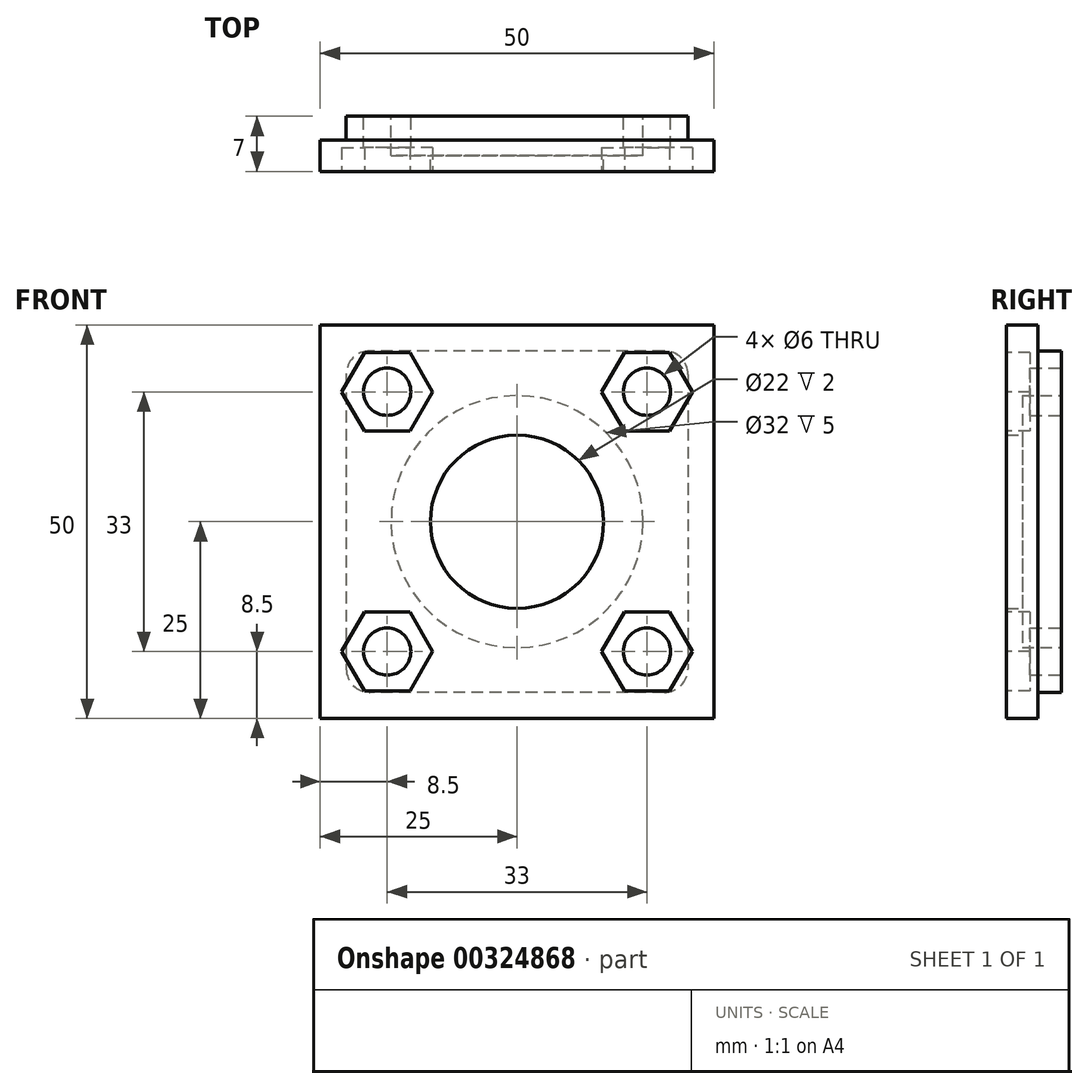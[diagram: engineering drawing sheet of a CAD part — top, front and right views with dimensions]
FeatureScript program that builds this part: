
annotation { "Feature Type Name" : "Feature", "Feature Type Description" : "" }
export const myFeature = defineFeature(function(context is Context, id is Id, definition is map)
    precondition{}
    {
        {
            var Q0;
            Q0=qCreatedBy(makeId("Front.planeOp"),FACE);
            var sketch = newSketch(context, id + "F0", { "sketchPlane" : qUnion([Q0])});
            skLineSegment(sketch, "E0.bottom", {"start": v(-25, 25) * mm, "end": v(25, 25) * mm});
            skLineSegment(sketch, "E0.top", {"start": v(-25, -25) * mm, "end": v(25, -25) * mm});
            skLineSegment(sketch, "E0.left", {"start": v(-25, 25) * mm, "end": v(-25, -25) * mm});
            skLineSegment(sketch, "E0.right", {"start": v(25, 25) * mm, "end": v(25, -25) * mm});
            skPoint(sketch, "E0.middle", {"position": v(0, 0) * mm});
            skSolve(sketch);
        }
        {
            var Q0;
            Q0=makeQuery(id+"F0.imprint","IMPRINT",FACE,{"disambiguationData":[TD([[makeQuery(id+"F0.imprint","IMPRINT",EDGE,{"derivedFrom":sQuery(id+"F0.wireOp",EDGE,"E0.bottom")}),-1.0]])]});
            extrude(context, id + "F1", {"entities" : qUnion([Q0]), "oppositeDirection" : true, "depth" : 4 * mm});
        }
        {
            var Q0;
            Q0=makeQuery(id+"F1.opExtrude","CAP_FACE",FACE,{"disambiguationData":[OSD([sQuery(id+"F0.wireOp",EDGE,"E0.bottom"),sQuery(id+"F0.wireOp",EDGE,"E0.top"),sQuery(id+"F0.wireOp",EDGE,"E0.left"),sQuery(id+"F0.wireOp",EDGE,"E0.right")])],"isStart":false});
            var sketch = newSketch(context, id + "F2", { "sketchPlane" : qUnion([Q0])});
            skLineSegment(sketch, "E1.bottom", {"start": v(-21.7, 21.7) * mm, "end": v(21.7, 21.7) * mm});
            skLineSegment(sketch, "E1.top", {"start": v(-21.7, -21.7) * mm, "end": v(21.7, -21.7) * mm});
            skLineSegment(sketch, "E1.left", {"start": v(-21.7, 21.7) * mm, "end": v(-21.7, -21.7) * mm});
            skLineSegment(sketch, "E1.right", {"start": v(21.7, 21.7) * mm, "end": v(21.7, -21.7) * mm});
            skPoint(sketch, "E1.middle", {"position": v(0, 0) * mm});
            skSolve(sketch);
        }
        {
            var Q0;
            Q0=makeQuery(id+"F2.imprint","IMPRINT",FACE,{"disambiguationData":[TD([[makeQuery(id+"F2.imprint","IMPRINT",EDGE,{"derivedFrom":sQuery(id+"F2.wireOp",EDGE,"E1.bottom")}),-1.0]])]});
            extrude(context, id + "F3", {"entities" : qUnion([Q0]), "operationType" : NewBodyOperationType.ADD, "depth" : 3 * mm});
        }
        {
            var Q0;
            Q0=makeQuery(id+"F3.opExtrude","CAP_FACE",FACE,{"disambiguationData":[OSD([sQuery(id+"F2.wireOp",EDGE,"E1.bottom"),sQuery(id+"F2.wireOp",EDGE,"E1.top"),sQuery(id+"F2.wireOp",EDGE,"E1.left"),sQuery(id+"F2.wireOp",EDGE,"E1.right")])],"isStart":false});
            var sketch = newSketch(context, id + "F4", { "sketchPlane" : qUnion([Q0])});
            skLineSegment(sketch, "E2", {"start": v(-21.7, 21.7) * mm, "end": v(21.7, -21.7) * mm, "construction": true});
            skLineSegment(sketch, "E3", {"start": v(21.7, 21.7) * mm, "end": v(-21.7, -21.7) * mm, "construction": true});
            skLineSegment(sketch, "E4.bottom", {"start": v(-16.5, 16.5) * mm, "end": v(16.5, 16.5) * mm, "construction": true});
            skLineSegment(sketch, "E4.top", {"start": v(-16.5, -16.5) * mm, "end": v(16.5, -16.5) * mm, "construction": true});
            skLineSegment(sketch, "E4.left", {"start": v(-16.5, 16.5) * mm, "end": v(-16.5, -16.5) * mm, "construction": true});
            skLineSegment(sketch, "E4.right", {"start": v(16.5, 16.5) * mm, "end": v(16.5, -16.5) * mm, "construction": true});
            skPoint(sketch, "E4.middle", {"position": v(0, 0) * mm});
            skCircle(sketch, "E5", {"center": v(-16.5, 16.5) * mm, "radius": 3 * mm});
            skCircle(sketch, "E6", {"center": v(16.5, 16.5) * mm, "radius": 3 * mm});
            skCircle(sketch, "E7", {"center": v(-16.5, -16.5) * mm, "radius": 3 * mm});
            skCircle(sketch, "E8", {"center": v(16.5, -16.5) * mm, "radius": 3 * mm});
            skCircle(sketch, "E9", {"center": v(0, 0) * mm, "radius": 11 * mm});
            skSolve(sketch);
        }
        {
            var Q0;
            Q0=makeQuery(id+"F4.imprint","IMPRINT",FACE,{"disambiguationData":[TD([[makeQuery(id+"F4.imprint","IMPRINT",EDGE,{"derivedFrom":sQuery(id+"F4.wireOp",EDGE,"E5")}),1.0]])]});
            var Q1;
            Q1=makeQuery(id+"F4.imprint","IMPRINT",FACE,{"disambiguationData":[TD([[makeQuery(id+"F4.imprint","IMPRINT",EDGE,{"derivedFrom":sQuery(id+"F4.wireOp",EDGE,"E6")}),1.0]])]});
            var Q2;
            Q2=makeQuery(id+"F4.imprint","IMPRINT",FACE,{"disambiguationData":[TD([[makeQuery(id+"F4.imprint","IMPRINT",EDGE,{"derivedFrom":sQuery(id+"F4.wireOp",EDGE,"E8")}),1.0]])]});
            var Q3;
            Q3=makeQuery(id+"F4.imprint","IMPRINT",FACE,{"disambiguationData":[TD([[makeQuery(id+"F4.imprint","IMPRINT",EDGE,{"derivedFrom":sQuery(id+"F4.wireOp",EDGE,"E7")}),1.0]])]});
            var Q4;
            Q4=makeQuery(id+"F4.imprint","IMPRINT",FACE,{"disambiguationData":[TD([[makeQuery(id+"F4.imprint","IMPRINT",EDGE,{"derivedFrom":sQuery(id+"F4.wireOp",EDGE,"E9")}),1.0]])]});
            extrude(context, id + "F5", {"entities" : qUnion([Q0, Q1, Q2, Q3, Q4]), "operationType" : NewBodyOperationType.REMOVE, "oppositeDirection" : true, "depth" : 25 * mm});
        }
        {
            var Q0;
            Q0=makeQuery(id+"F1.opExtrude","CAP_FACE",FACE,{"disambiguationData":[OSD([sQuery(id+"F0.wireOp",EDGE,"E0.bottom"),sQuery(id+"F0.wireOp",EDGE,"E0.top"),sQuery(id+"F0.wireOp",EDGE,"E0.left"),sQuery(id+"F0.wireOp",EDGE,"E0.right")])],"isStart":true});
            var sketch = newSketch(context, id + "F6", { "sketchPlane" : qUnion([Q0])});
            skCircle(sketch, "E10.cCircle", {"center": v(-16.5, 16.5) * mm, "radius": 5 * mm, "construction": true});
            skLineSegment(sketch, "E10.0", {"start": v(-13.61, 11.5) * mm, "end": v(-19.39, 11.5) * mm});
            skLineSegment(sketch, "E10.1", {"start": v(-19.39, 11.5) * mm, "end": v(-22.27, 16.5) * mm});
            skLineSegment(sketch, "E10.2", {"start": v(-22.27, 16.5) * mm, "end": v(-19.39, 21.5) * mm});
            skLineSegment(sketch, "E10.3", {"start": v(-19.39, 21.5) * mm, "end": v(-13.61, 21.5) * mm});
            skLineSegment(sketch, "E10.4", {"start": v(-13.61, 21.5) * mm, "end": v(-10.73, 16.5) * mm});
            skLineSegment(sketch, "E10.5", {"start": v(-10.73, 16.5) * mm, "end": v(-13.61, 11.5) * mm});
            skPoint(sketch, "E10.0.midPoint", {"position": v(-16.5, 11.5) * mm});
            skCircle(sketch, "E11.cCircle", {"center": v(-16.5, -16.5) * mm, "radius": 5 * mm, "construction": true});
            skLineSegment(sketch, "E11.0", {"start": v(-13.61, -21.5) * mm, "end": v(-19.39, -21.5) * mm});
            skLineSegment(sketch, "E11.1", {"start": v(-19.39, -21.5) * mm, "end": v(-22.27, -16.5) * mm});
            skLineSegment(sketch, "E11.2", {"start": v(-22.27, -16.5) * mm, "end": v(-19.39, -11.5) * mm});
            skLineSegment(sketch, "E11.3", {"start": v(-19.39, -11.5) * mm, "end": v(-13.61, -11.5) * mm});
            skLineSegment(sketch, "E11.4", {"start": v(-13.61, -11.5) * mm, "end": v(-10.73, -16.5) * mm});
            skLineSegment(sketch, "E11.5", {"start": v(-10.73, -16.5) * mm, "end": v(-13.61, -21.5) * mm});
            skPoint(sketch, "E11.0.midPoint", {"position": v(-16.5, -21.5) * mm});
            skCircle(sketch, "E12.cCircle", {"center": v(16.5, 16.5) * mm, "radius": 5 * mm, "construction": true});
            skLineSegment(sketch, "E12.0", {"start": v(13.61, 21.5) * mm, "end": v(19.39, 21.5) * mm});
            skLineSegment(sketch, "E12.1", {"start": v(19.39, 21.5) * mm, "end": v(22.27, 16.5) * mm});
            skLineSegment(sketch, "E12.2", {"start": v(22.27, 16.5) * mm, "end": v(19.39, 11.5) * mm});
            skLineSegment(sketch, "E12.3", {"start": v(19.39, 11.5) * mm, "end": v(13.61, 11.5) * mm});
            skLineSegment(sketch, "E12.4", {"start": v(13.61, 11.5) * mm, "end": v(10.73, 16.5) * mm});
            skLineSegment(sketch, "E12.5", {"start": v(10.73, 16.5) * mm, "end": v(13.61, 21.5) * mm});
            skPoint(sketch, "E12.0.midPoint", {"position": v(16.5, 21.5) * mm});
            skCircle(sketch, "E13.cCircle", {"center": v(16.5, -16.5) * mm, "radius": 5 * mm, "construction": true});
            skLineSegment(sketch, "E13.0", {"start": v(19.39, -21.5) * mm, "end": v(13.61, -21.5) * mm});
            skLineSegment(sketch, "E13.1", {"start": v(13.61, -21.5) * mm, "end": v(10.73, -16.5) * mm});
            skLineSegment(sketch, "E13.2", {"start": v(10.73, -16.5) * mm, "end": v(13.61, -11.5) * mm});
            skLineSegment(sketch, "E13.3", {"start": v(13.61, -11.5) * mm, "end": v(19.39, -11.5) * mm});
            skLineSegment(sketch, "E13.4", {"start": v(19.39, -11.5) * mm, "end": v(22.27, -16.5) * mm});
            skLineSegment(sketch, "E13.5", {"start": v(22.27, -16.5) * mm, "end": v(19.39, -21.5) * mm});
            skPoint(sketch, "E13.0.midPoint", {"position": v(16.5, -21.5) * mm});
            skSolve(sketch);
        }
        {
            var Q0;
            Q0=makeQuery(id+"F6.imprint","IMPRINT",FACE,{"disambiguationData":[TD([[makeQuery(id+"F6.imprint","IMPRINT",EDGE,{"derivedFrom":sQuery(id+"F6.wireOp",EDGE,"E10.0")}),-1.0]])]});
            var Q1;
            Q1=makeQuery(id+"F6.imprint","IMPRINT",FACE,{"disambiguationData":[TD([[makeQuery(id+"F6.imprint","IMPRINT",EDGE,{"derivedFrom":sQuery(id+"F6.wireOp",EDGE,"E12.0")}),-1.0]])]});
            var Q2;
            Q2=makeQuery(id+"F6.imprint","IMPRINT",FACE,{"disambiguationData":[TD([[makeQuery(id+"F6.imprint","IMPRINT",EDGE,{"derivedFrom":sQuery(id+"F6.wireOp",EDGE,"E13.0")}),-1.0]])]});
            var Q3;
            Q3=makeQuery(id+"F6.imprint","IMPRINT",FACE,{"disambiguationData":[TD([[makeQuery(id+"F6.imprint","IMPRINT",EDGE,{"derivedFrom":sQuery(id+"F6.wireOp",EDGE,"E11.0")}),-1.0]])]});
            extrude(context, id + "F7", {"entities" : qUnion([Q0, Q1, Q2, Q3]), "operationType" : NewBodyOperationType.REMOVE, "oppositeDirection" : true, "depth" : 3 * mm});
        }
        {
            var Q0;
            Q0=makeQuery(id+"F3.opExtrude","CAP_FACE",FACE,{"disambiguationData":[OSD([sQuery(id+"F2.wireOp",EDGE,"E1.bottom"),sQuery(id+"F2.wireOp",EDGE,"E1.top"),sQuery(id+"F2.wireOp",EDGE,"E1.left"),sQuery(id+"F2.wireOp",EDGE,"E1.right")])],"isStart":false});
            var sketch = newSketch(context, id + "F8", { "sketchPlane" : qUnion([Q0])});
            skCircle(sketch, "E14", {"center": v(0, 0) * mm, "radius": 16 * mm});
            skSolve(sketch);
        }
        {
            var Q0;
            Q0=makeQuery(id+"F8.imprint","IMPRINT",FACE,{"disambiguationData":[TD([[makeQuery(id+"F8.imprint","IMPRINT",EDGE,{"derivedFrom":sQuery(id+"F8.wireOp",EDGE,"E14")}),1.0]])]});
            extrude(context, id + "F9", {"entities" : qUnion([Q0]), "operationType" : NewBodyOperationType.REMOVE, "oppositeDirection" : true, "depth" : 5 * mm});
        }
        {
            var Q0;
            Q0=makeQuery(id+"F3.opExtrude","SWEPT_EDGE",EDGE,{"disambiguationData":[OSD([sQuery(id+"F2.wireOp",EDGE,"E1.bottom"),sQuery(id+"F2.wireOp",EDGE,"E1.left")])]});
            var Q1;
            Q1=makeQuery(id+"F3.opExtrude","SWEPT_EDGE",EDGE,{"disambiguationData":[OSD([sQuery(id+"F2.wireOp",EDGE,"E1.top"),sQuery(id+"F2.wireOp",EDGE,"E1.left")])]});
            var Q2;
            Q2=makeQuery(id+"F3.opExtrude","SWEPT_EDGE",EDGE,{"disambiguationData":[OSD([sQuery(id+"F2.wireOp",EDGE,"E1.top"),sQuery(id+"F2.wireOp",EDGE,"E1.right")])]});
            var Q3;
            Q3=makeQuery(id+"F3.opExtrude","SWEPT_EDGE",EDGE,{"disambiguationData":[OSD([sQuery(id+"F2.wireOp",EDGE,"E1.bottom"),sQuery(id+"F2.wireOp",EDGE,"E1.right")])]});
            fillet(context, id + "F10", {"entities" : qUnion([Q0, Q1, Q2, Q3]), "radius" : 3 * mm, "tangentPropagation" : true, "allowEdgeOverflow" : false});
        }
    });
